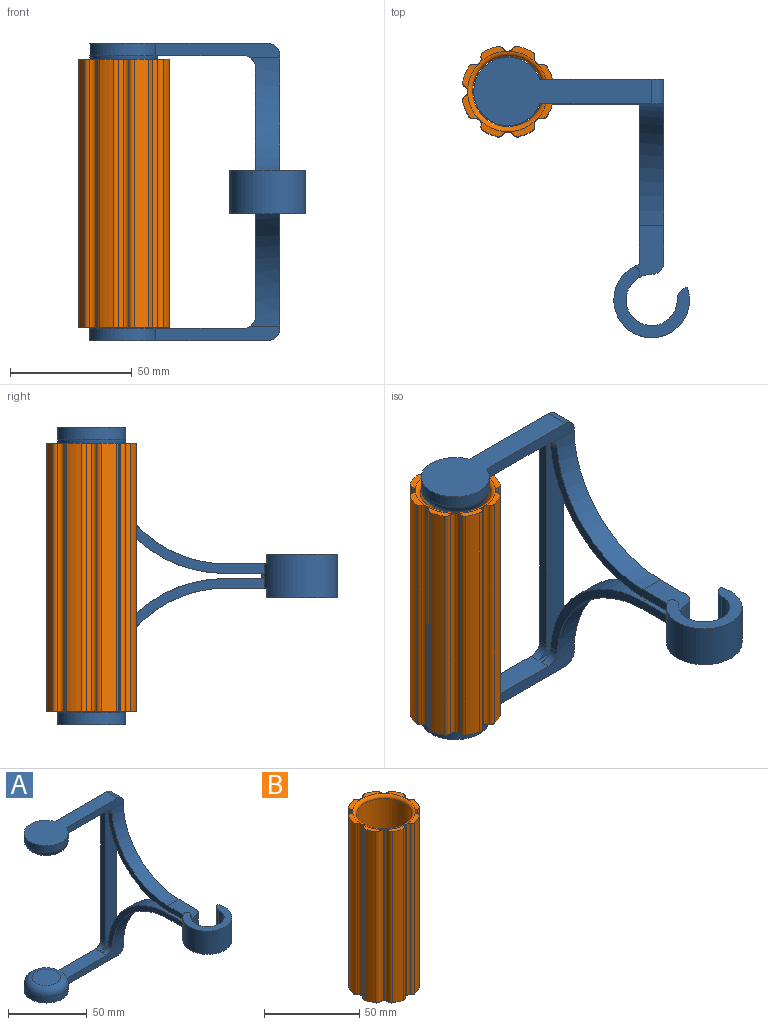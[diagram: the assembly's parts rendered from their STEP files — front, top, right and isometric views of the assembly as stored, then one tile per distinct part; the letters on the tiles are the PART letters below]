
ASSEMBLY  parts=2 mates=1
PART A: 61 faces, bbox 89.7x116.2x122 mm
  f0: plane 70x56mm, normal (1,0,0), area 391.2mm2, adj f8,f20,f22,f33,f36,f49,f52,f55
  f1: plane 112x5mm, normal (1,0,0), area 448.4mm2, adj f9,f19,f20,f41,f54,f55
  f2: plane 69.68x50mm, normal (-1,0,0), area 374mm2, adj f22,f27,f36,f49,f52,f60
  f3: plane 102x4mm, normal (-1,0,0), area 408mm2, adj f9,f41,f57,f58
  f4: plane 50.92x6mm, normal (0,-1,0), area 262.2mm2, adj f13,f14,f15,f16,f19,f37,f59
  f5: cylinder r=14mm len=28mm, axis (0,0,-1), area 388.7mm2, adj f7,f8,f9,f11
  f6: plane 18x18mm, normal (0,0,1), area 254.5mm2, adj f11
  f7: plane 73x28mm, normal (0,0,-1), area 1068.8mm2, adj f5,f8,f9,f20
  f8: plane 50.92x6mm, normal (0,-1,0), area 262.2mm2, adj f0,f5,f7,f10,f20,f36,f60
  f9: plane 122x50.92mm, normal (0,1,0), area 1629.2mm2, adj f1,f3,f5,f7,f10,f14,f15,f16
  f10: plane 40.92x10mm, normal (0,0,1), area 363mm2, adj f8,f9,f11,f39,f40,f41,f57,f60
  f11: torus R=9mm, axis (0,0,1), area 601.2mm2, adj f5,f6,f10
  f12: plane 69.68x50mm, normal (-1,0,0), area 374mm2, adj f21,f27,f37,f48,f53,f59
  f13: plane 70x56mm, normal (1,0,0), area 391.2mm2, adj f4,f19,f21,f33,f37,f48,f53,f54
  f14: cylinder r=14mm len=28mm, axis (0,0,-1), area 388.7mm2, adj f4,f9,f15,f18
  f15: plane 73x28mm, normal (0,0,1), area 1068.8mm2, adj f4,f9,f14,f19
  f16: plane 40.92x10mm, normal (0,0,-1), area 363mm2, adj f4,f9,f18,f41,f42,f44,f58,f59
  f17: plane 18x18mm, normal (0,0,-1), area 254.5mm2, adj f18
  f18: torus R=9mm, axis (0,0,1), area 601.2mm2, adj f14,f16,f17
  f19: cylinder r=5mm len=10mm, axis (0,-1,0), area 78.5mm2, adj f1,f4,f9,f13,f15
  f20: cylinder r=5mm len=10mm, axis (0,1,0), area 78.5mm2, adj f0,f1,f7,f8,f9
  f21: plane 22.34x13.04mm, normal (0,0,1), area 199.7mm2, adj f12,f13,f23,f25,f27,f32,f33,f35
  f22: plane 22.34x13.04mm, normal (0,0,-1), area 199.7mm2, adj f0,f2,f25,f26,f27,f31,f33,f34
  f23: plane 4x1.04mm, normal (1,0,0), area 4.2mm2, adj f21,f28,f32,f35
  f24: plane 18x0.78mm, normal (-0.34,0.94,0), area 14.9mm2, adj f27,f28,f29,f30
  f25: cylinder r=10.5mm len=21mm, axis (0,0,-1), area 837.4mm2, adj f21,f22,f28,f29,f30,f31,f32,f33
  f26: plane 4x1.04mm, normal (1,0,0), area 4.2mm2, adj f22,f29,f31,f34
  f27: cylinder r=15.5mm len=31mm, axis (0,0,-1), area 1293.6mm2, adj f2,f12,f21,f22,f24,f28,f29,f34
  f28: plane 31x29.04mm, normal (0,0,1), area 297.3mm2, adj f23,f24,f25,f27,f30,f32,f35
  f29: plane 31x29.04mm, normal (0,0,-1), area 297.3mm2, adj f24,f25,f26,f27,f30,f31,f34
  f30: cylinder r=5mm len=18mm, axis (0,0,-1), area 111.8mm2, adj f24,f25,f28,f29
  f31: cylinder r=5mm len=4mm, axis (0,0,-1), area 11.5mm2, adj f22,f25,f26,f29
  f32: cylinder r=5mm len=4mm, axis (0,0,-1), area 11.5mm2, adj f21,f23,f25,f28
  f33: cylinder r=5mm len=10mm, axis (0,0,-1), area 78.5mm2, adj f0,f13,f21,f22,f25
  f34: cylinder r=2mm len=4mm, axis (0,0,-1), area 16.9mm2, adj f22,f26,f27,f29
  f35: cylinder r=2mm len=4mm, axis (0,0,-1), area 16.9mm2, adj f21,f23,f27,f28
  f36: cylinder r=50mm len=50mm, axis (1,0,0), area 789.4mm2, adj f0,f2,f8,f22,f60
  f37: cylinder r=50mm len=50mm, axis (-1,0,0), area 789.4mm2, adj f4,f12,f13,f21,f59
  f38: plane 2x1.06mm, normal (1,0,0), area 2.1mm2, adj f27,f48,f49,f50
  f39: plane 2x1mm, normal (1,0,0), area 2mm2, adj f10,f40,f41,f43
  f40: plane 11x2mm, normal (0,1,0), area 14.5mm2, adj f10,f39,f43,f47,f52,f60
  f41: plane 114x15mm, normal (0,-1,0), area 1133.9mm2, adj f1,f3,f10,f16,f39,f43,f44,f45
  f42: plane 11x2mm, normal (0,1,0), area 14.5mm2, adj f16,f44,f45,f46,f53,f59
  f43: plane 5x2mm, normal (0,0,1), area 10mm2, adj f39,f40,f41,f47
  f44: plane 2x1mm, normal (1,0,0), area 2mm2, adj f16,f41,f42,f45
  f45: plane 5x2mm, normal (0,0,-1), area 10mm2, adj f41,f42,f44,f46
  f46: cylinder r=1mm len=2mm, axis (0,-1,0), area 4.7mm2, adj f41,f42,f45,f54
  f47: cylinder r=1mm len=2mm, axis (0,1,0), area 4.7mm2, adj f40,f41,f43,f55
  f48: plane 16.89x10mm, normal (0,0,-1), area 153mm2, adj f12,f13,f38,f50,f51,f53,f56
  f49: plane 16.89x10mm, normal (0,0,1), area 153mm2, adj f0,f2,f38,f50,f51,f52,f56
  f50: cylinder r=14.5mm len=5mm, axis (0,0,-1), area 10.2mm2, adj f38,f48,f49,f51
  f51: cylinder r=1mm len=2mm, axis (0,0,-1), area 4.7mm2, adj f48,f49,f50,f56
  f52: cylinder r=54mm len=54mm, axis (1,0,0), area 852.2mm2, adj f0,f2,f40,f49,f55,f60
  f53: cylinder r=54mm len=54mm, axis (-1,0,0), area 852.2mm2, adj f12,f13,f42,f48,f54,f59
  f54: cylinder r=1mm len=5mm, axis (-1,0,0), area 14.1mm2, adj f1,f13,f41,f46,f53
  f55: cylinder r=1mm len=5mm, axis (-1,0,0), area 14.1mm2, adj f0,f1,f41,f47,f52
  f56: cylinder r=1mm len=5mm, axis (1,0,0), area 14.1mm2, adj f0,f13,f48,f49,f51
  f57: cylinder r=5mm len=5mm, axis (0,-1,0), area 31.4mm2, adj f3,f9,f10,f41
  f58: cylinder r=5mm len=5mm, axis (0,1,0), area 31.4mm2, adj f3,f9,f16,f41
  f59: cylinder r=5mm len=5mm, axis (0,1,0), area 31.4mm2, adj f4,f12,f16,f37,f42,f53
  f60: cylinder r=5mm len=5mm, axis (0,-1,0), area 31.4mm2, adj f2,f8,f10,f36,f40,f52
PART B: 67 faces, bbox 38.8x38.8x110 mm
  f0: plane 11.66x6.9mm, normal (0,0,1), area 24.3mm2, adj f25,f44,f45,f59,f60,f66
  f1: plane 11.66x6.9mm, normal (0,0,1), area 24.3mm2, adj f23,f42,f43,f57,f58,f66
  f2: plane 11.66x6.9mm, normal (0,0,1), area 24.3mm2, adj f21,f40,f41,f55,f56,f66
  f3: plane 11.66x6.9mm, normal (0,0,1), area 24.3mm2, adj f19,f38,f39,f53,f54,f66
  f4: plane 11.66x6.9mm, normal (0,0,1), area 24.3mm2, adj f17,f36,f37,f51,f52,f66
  f5: plane 11.66x6.9mm, normal (0,0,1), area 24.3mm2, adj f15,f34,f35,f49,f50,f66
  f6: plane 11.66x6.9mm, normal (0,0,1), area 24.3mm2, adj f29,f33,f48,f63,f64,f66
  f7: plane 11.66x6.9mm, normal (0,0,-1), area 24.3mm2, adj f27,f46,f47,f61,f62,f65
  f8: plane 11.66x6.9mm, normal (0,0,-1), area 24.3mm2, adj f29,f33,f48,f63,f64,f65
  f9: plane 11.66x6.9mm, normal (0,0,-1), area 24.3mm2, adj f15,f34,f35,f49,f50,f65
  f10: plane 11.66x6.9mm, normal (0,0,-1), area 24.3mm2, adj f17,f36,f37,f51,f52,f65
  f11: plane 11.66x6.9mm, normal (0,0,-1), area 24.3mm2, adj f19,f38,f39,f53,f54,f65
  f12: plane 11.66x6.9mm, normal (0,0,-1), area 24.3mm2, adj f21,f40,f41,f55,f56,f65
  f13: plane 11.66x6.9mm, normal (0,0,-1), area 24.3mm2, adj f23,f42,f43,f57,f58,f65
  f14: plane 110x0.01mm, normal (0,1,0), area 1.2mm2, adj f33,f34,f65,f66
  f15: cylinder r=19mm len=110mm, axis (0,0,-1), area 700.7mm2, adj f5,f9,f49,f50
  f16: plane 110x0.01mm, normal (-0.71,0.71,0), area 1.2mm2, adj f35,f36,f65,f66
  f17: cylinder r=19mm len=110mm, axis (0,0,-1), area 700.7mm2, adj f4,f10,f51,f52
  f18: plane 110x0.01mm, normal (-1,0,0), area 1.2mm2, adj f37,f38,f65,f66
  f19: cylinder r=19mm len=110mm, axis (0,0,-1), area 700.7mm2, adj f3,f11,f53,f54
  f20: plane 110x0.01mm, normal (-0.71,-0.71,0), area 1.2mm2, adj f39,f40,f65,f66
  f21: cylinder r=19mm len=110mm, axis (0,0,-1), area 700.7mm2, adj f2,f12,f55,f56
  f22: plane 110x0.01mm, normal (0,-1,0), area 1.2mm2, adj f41,f42,f65,f66
  f23: cylinder r=19mm len=110mm, axis (0,0,-1), area 700.7mm2, adj f1,f13,f57,f58
  f24: plane 110x0.01mm, normal (0.71,-0.71,0), area 1.2mm2, adj f43,f44,f65,f66
  f25: cylinder r=19mm len=110mm, axis (0,0,-1), area 700.7mm2, adj f0,f32,f59,f60
  f26: plane 110x0.01mm, normal (1,0,0), area 1.2mm2, adj f45,f46,f65,f66
  f27: cylinder r=19mm len=110mm, axis (0,0,-1), area 700.7mm2, adj f7,f31,f61,f62
  f28: plane 110x0.01mm, normal (0.71,0.71,0), area 1.2mm2, adj f47,f48,f65,f66
  f29: cylinder r=19mm len=110mm, axis (0,0,-1), area 700.7mm2, adj f6,f8,f63,f64
  f30: cylinder r=14.5mm len=106mm, axis (0,0,-1), area 9657.3mm2, adj f65,f66
  f31: plane 11.66x6.9mm, normal (0,0,1), area 24.3mm2, adj f27,f46,f47,f61,f62,f66
  f32: plane 11.66x6.9mm, normal (0,0,-1), area 24.3mm2, adj f25,f44,f45,f59,f60,f65
  f33: cylinder r=2.5mm len=110mm, axis (0,0,-1), area 275.2mm2, adj f6,f8,f14,f64
  f34: cylinder r=2.5mm len=110mm, axis (0,0,-1), area 275.2mm2, adj f5,f9,f14,f49
  f35: cylinder r=2.5mm len=110mm, axis (0,0,-1), area 275.2mm2, adj f5,f9,f16,f50
  f36: cylinder r=2.5mm len=110mm, axis (0,0,-1), area 275.2mm2, adj f4,f10,f16,f51
  f37: cylinder r=2.5mm len=110mm, axis (0,0,-1), area 275.2mm2, adj f4,f10,f18,f52
  f38: cylinder r=2.5mm len=110mm, axis (0,0,-1), area 275.2mm2, adj f3,f11,f18,f53
  f39: cylinder r=2.5mm len=110mm, axis (0,0,-1), area 275.2mm2, adj f3,f11,f20,f54
  f40: cylinder r=2.5mm len=110mm, axis (0,0,-1), area 275.2mm2, adj f2,f12,f20,f55
  f41: cylinder r=2.5mm len=110mm, axis (0,0,-1), area 275.2mm2, adj f2,f12,f22,f56
  f42: cylinder r=2.5mm len=110mm, axis (0,0,-1), area 275.2mm2, adj f1,f13,f22,f57
  f43: cylinder r=2.5mm len=110mm, axis (0,0,-1), area 275.2mm2, adj f1,f13,f24,f58
  f44: cylinder r=2.5mm len=110mm, axis (0,0,-1), area 275.2mm2, adj f0,f24,f32,f59
  f45: cylinder r=2.5mm len=110mm, axis (0,0,-1), area 275.2mm2, adj f0,f26,f32,f60
  f46: cylinder r=2.5mm len=110mm, axis (0,0,-1), area 275.2mm2, adj f7,f26,f31,f61
  f47: cylinder r=2.5mm len=110mm, axis (0,0,-1), area 275.2mm2, adj f7,f28,f31,f62
  f48: cylinder r=2.5mm len=110mm, axis (0,0,-1), area 275.2mm2, adj f6,f8,f28,f63
  f49: cylinder r=2mm len=110mm, axis (0,0,1), area 269.7mm2, adj f5,f9,f15,f34
  f50: cylinder r=2mm len=110mm, axis (0,0,1), area 269.7mm2, adj f5,f9,f15,f35
  f51: cylinder r=2mm len=110mm, axis (0,0,1), area 269.7mm2, adj f4,f10,f17,f36
  f52: cylinder r=2mm len=110mm, axis (0,0,1), area 269.7mm2, adj f4,f10,f17,f37
  f53: cylinder r=2mm len=110mm, axis (0,0,1), area 269.7mm2, adj f3,f11,f19,f38
  f54: cylinder r=2mm len=110mm, axis (0,0,1), area 269.7mm2, adj f3,f11,f19,f39
  f55: cylinder r=2mm len=110mm, axis (0,0,1), area 269.7mm2, adj f2,f12,f21,f40
  f56: cylinder r=2mm len=110mm, axis (0,0,1), area 269.7mm2, adj f2,f12,f21,f41
  f57: cylinder r=2mm len=110mm, axis (0,0,1), area 269.7mm2, adj f1,f13,f23,f42
  f58: cylinder r=2mm len=110mm, axis (0,0,1), area 269.7mm2, adj f1,f13,f23,f43
  f59: cylinder r=2mm len=110mm, axis (0,0,1), area 269.7mm2, adj f0,f25,f32,f44
  f60: cylinder r=2mm len=110mm, axis (0,0,1), area 269.7mm2, adj f0,f25,f32,f45
  f61: cylinder r=2mm len=110mm, axis (0,0,1), area 269.7mm2, adj f7,f27,f31,f46
  f62: cylinder r=2mm len=110mm, axis (0,0,1), area 269.7mm2, adj f7,f27,f31,f47
  f63: cylinder r=2mm len=110mm, axis (0,0,1), area 269.7mm2, adj f6,f8,f29,f48
  f64: cylinder r=2mm len=110mm, axis (0,0,1), area 269.7mm2, adj f6,f8,f29,f33
  f65: torus R=16.5mm, axis (0,0,1), area 300.6mm2, adj f7,f8,f9,f10,f11,f12,f13,f14
  f66: torus R=16.5mm, axis (0,0,1), area 300.6mm2, adj f0,f1,f2,f3,f4,f5,f6,f14
PLACE A t=(-126.99,-51.5,-9.34)mm
PLACE B t=(-126.99,4.54,-3.88)mm
MATE revolute B.f30 <-> A.f14  axis (0,0,1) through (-126.99,4.54,104.12)mm
